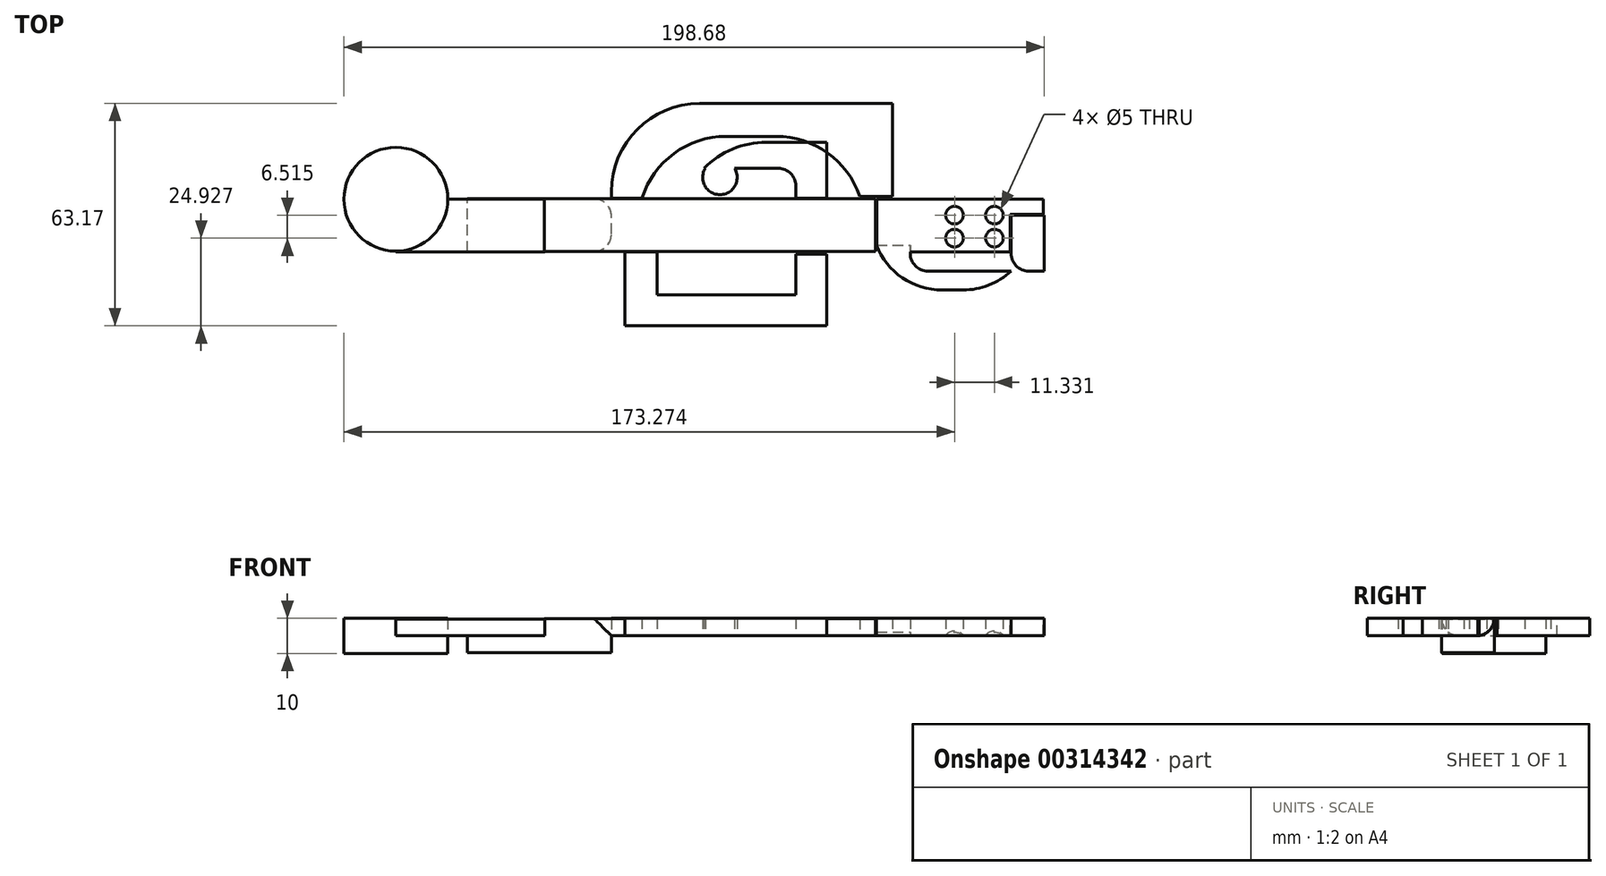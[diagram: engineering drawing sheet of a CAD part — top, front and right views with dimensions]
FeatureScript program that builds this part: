
annotation { "Feature Type Name" : "Feature", "Feature Type Description" : "" }
export const myFeature = defineFeature(function(context is Context, id is Id, definition is map)
    precondition{}
    {
        {
            var Q0;
            Q0=qCreatedBy(makeId("Front.planeOp"),FACE);
            var sketch = newSketch(context, id + "F0", { "sketchPlane" : qUnion([Q0])});
            skLineSegment(sketch, "E0.bottom", {"start": v(0, 0) * mm, "end": v(74.96, 0) * mm});
            skLineSegment(sketch, "E0.top", {"start": v(0, 4.82) * mm, "end": v(74.96, 4.82) * mm});
            skLineSegment(sketch, "E0.left", {"start": v(0, 0) * mm, "end": v(0, 4.82) * mm});
            skLineSegment(sketch, "E0.right", {"start": v(74.96, 0) * mm, "end": v(74.96, 4.82) * mm});
            skLineSegment(sketch, "E1.bottom", {"start": v(0, 4.82) * mm, "end": v(-19.08, 4.82) * mm});
            skLineSegment(sketch, "E1.top", {"start": v(0, -4.82) * mm, "end": v(-19.08, -4.82) * mm});
            skLineSegment(sketch, "E1.left", {"start": v(0, 4.82) * mm, "end": v(0, -4.82) * mm});
            skLineSegment(sketch, "E1.right", {"start": v(-19.08, 4.82) * mm, "end": v(-19.08, -4.82) * mm});
            skPoint(sketch, "E2.oppositeSnap0", {"position": v(-19.08, 0) * mm});
            skLineSegment(sketch, "E2.bottom", {"start": v(-19.08, -4.82) * mm, "end": v(-40.9, -4.82) * mm});
            skLineSegment(sketch, "E2.top", {"start": v(-19.08, 0) * mm, "end": v(-40.9, 0) * mm});
            skLineSegment(sketch, "E2.left", {"start": v(-19.08, -4.82) * mm, "end": v(-19.08, 0) * mm});
            skLineSegment(sketch, "E2.right", {"start": v(-40.9, -4.82) * mm, "end": v(-40.9, 0) * mm});
            skSolve(sketch);
        }
        {
            var Q0;
            Q0 = qSketchRegion(id + "F0", true);
            extrude(context, id + "F1", {"entities" : qUnion([Q0]), "endBound" : BoundingType.SYMMETRIC, "depth" : 15 * mm});
        }
        {
            var Q0;
            Q0=makeQuery(id+"F1.opExtrude","CAP_EDGE",EDGE,{"disambiguationData":[OSD([sQuery(id+"F0.wireOp",EDGE,"E0.bottom")])],"isStart":false});
            var Q1;
            Q1=makeQuery(id+"F1.opExtrude","CAP_EDGE",EDGE,{"disambiguationData":[OSD([sQuery(id+"F0.wireOp",EDGE,"E0.bottom")])],"isStart":true});
            var Q2;
            Q2=makeQuery(id+"F1.opExtrude","CAP_EDGE",EDGE,{"disambiguationData":[OSD([sQuery(id+"F0.wireOp",EDGE,"E1.left")])],"isStart":false});
            var Q3;
            Q3=makeQuery(id+"F1.opExtrude","CAP_EDGE",EDGE,{"disambiguationData":[OSD([sQuery(id+"F0.wireOp",EDGE,"E1.left")])],"isStart":true});
            fillet(context, id + "F2", {"entities" : qUnion([Q0, Q1, Q2, Q3]), "radius" : 5 * mm, "tangentPropagation" : true, "allowEdgeOverflow" : false});
        }
        {
            var Q0;
            Q0=qCreatedBy(makeId("Top.planeOp"),FACE);
            var sketch = newSketch(context, id + "F3", { "sketchPlane" : qUnion([Q0])});
            skLineSegment(sketch, "E3.bottom", {"start": v(-18.98, -7.65) * mm, "end": v(-61.19, -7.65) * mm});
            skLineSegment(sketch, "E3.top", {"start": v(-18.98, 7.37) * mm, "end": v(-61.19, 7.37) * mm});
            skLineSegment(sketch, "E3.left", {"start": v(-18.98, -7.65) * mm, "end": v(-18.98, 7.37) * mm});
            skLineSegment(sketch, "E3.right", {"start": v(-61.19, -7.65) * mm, "end": v(-61.19, 7.37) * mm});
            skCircle(sketch, "E4", {"center": v(-61.19, 7.37) * mm, "radius": 14.73 * mm});
            skSolve(sketch);
        }
        {
            var Q0;
            {var subQ1=sQuery(id+"F3.wireOp",EDGE,"E3.bottom");Q0=makeQuery(id+"F3.imprint","IMPRINT",FACE,{"disambiguationData":[TD([[makeQuery(id+"F3.imprint","IMPRINT",EDGE,{"derivedFrom":subQ1}),-1.0]])]});}
            extrude(context, id + "F4", {"entities" : qUnion([Q0]), "operationType" : NewBodyOperationType.ADD, "depth" : 4.8 * mm});
        }
        {
            var Q0;
            {var subQ0=sQuery(id+"F3.wireOp",EDGE,"E3.right");var subQ1=sQuery(id+"F3.wireOp",EDGE,"E3.top");var subQ2=makeQuery(id+"F3.imprint","INTERSECT",VERTEX,{"derivedFrom":[subQ1,subQ0]});Q0=makeQuery(id+"F3.imprint","IMPRINT",FACE,{"disambiguationData":[TD([[makeQuery(id+"F3.imprint","IMPRINT",EDGE,{"disambiguationData":[TD([[subQ2,1.0]])],"derivedFrom":subQ1}),-1.0]])]});}
            var Q1;
            {var subQ0=sQuery(id+"F3.wireOp",EDGE,"E3.right");var subQ1=sQuery(id+"F3.wireOp",EDGE,"E3.top");var subQ2=makeQuery(id+"F3.imprint","INTERSECT",VERTEX,{"derivedFrom":[subQ1,subQ0]});Q1=makeQuery(id+"F3.imprint","IMPRINT",FACE,{"disambiguationData":[TD([[makeQuery(id+"F3.imprint","IMPRINT",EDGE,{"disambiguationData":[TD([[subQ2,1.0]])],"derivedFrom":subQ1}),1.0]])]});}
            var Q2;
            Q2=makeQuery(id+"F1.opExtrude","SWEPT_BODY",BODY,{"disambiguationData":[OSD([sQuery(id+"F0.wireOp",EDGE,"E0.bottom"),sQuery(id+"F0.wireOp",EDGE,"E0.top"),sQuery(id+"F0.wireOp",EDGE,"E0.right"),sQuery(id+"F0.wireOp",EDGE,"E1.bottom"),sQuery(id+"F0.wireOp",EDGE,"E1.top"),sQuery(id+"F0.wireOp",EDGE,"E1.left"),sQuery(id+"F0.wireOp",EDGE,"E1.right"),sQuery(id+"F0.wireOp",EDGE,"E2.bottom"),sQuery(id+"F0.wireOp",EDGE,"E2.top"),sQuery(id+"F0.wireOp",EDGE,"E2.right")])]});
            extrude(context, id + "F5", {"entities" : qUnion([Q0, Q1]), "operationType" : NewBodyOperationType.ADD, "endBound" : BoundingType.SYMMETRIC, "endBoundEntityBody" : qUnion([Q2]), "depth" : 10 * mm});
        }
        {
            var Q0;
            Q0=qCreatedBy(makeId("Top.planeOp"),FACE);
            var sketch = newSketch(context, id + "F6", { "sketchPlane" : qUnion([Q0])});
            skLineSegment(sketch, "E5.bottom", {"start": v(75.26, -7.65) * mm, "end": v(113.13, -7.65) * mm});
            skLineSegment(sketch, "E5.top", {"start": v(75.26, 7.37) * mm, "end": v(113.13, 7.37) * mm});
            skLineSegment(sketch, "E5.left", {"start": v(75.26, -7.65) * mm, "end": v(75.26, 7.37) * mm});
            skLineSegment(sketch, "E5.right", {"start": v(113.13, -7.65) * mm, "end": v(113.13, 7.37) * mm});
            skLineSegment(sketch, "E6.bottom", {"start": v(113.13, 7.37) * mm, "end": v(122.57, 7.37) * mm});
            skLineSegment(sketch, "E6.top", {"start": v(113.13, 3.12) * mm, "end": v(122.57, 3.12) * mm});
            skLineSegment(sketch, "E6.left", {"start": v(113.13, 7.37) * mm, "end": v(113.13, 3.12) * mm});
            skLineSegment(sketch, "E6.right", {"start": v(122.57, 7.37) * mm, "end": v(122.57, 3.12) * mm});
            skSolve(sketch);
        }
        {
            var Q0;
            Q0=makeQuery(id+"F6.imprint","IMPRINT",FACE,{"disambiguationData":[TD([[makeQuery(id+"F6.imprint","IMPRINT",EDGE,{"derivedFrom":sQuery(id+"F6.wireOp",EDGE,"E5.bottom")}),1.0]])]});
            var Q1;
            Q1=makeQuery(id+"F6.imprint","IMPRINT",FACE,{"disambiguationData":[TD([[makeQuery(id+"F6.imprint","IMPRINT",EDGE,{"derivedFrom":sQuery(id+"F6.wireOp",EDGE,"E6.bottom")}),-1.0]])]});
            extrude(context, id + "F7", {"entities" : qUnion([Q0, Q1]), "depth" : 5 * mm});
        }
        {
            var Q0;
            Q0=makeQuery(id+"F7.opExtrude","CAP_EDGE",EDGE,{"disambiguationData":[OSD([sQuery(id+"F6.wireOp",EDGE,"E5.bottom")])],"isStart":true});
            var Q1;
            Q1=makeQuery(id+"F7.opExtrude","CAP_EDGE",EDGE,{"disambiguationData":[OSD([sQuery(id+"F6.wireOp",EDGE,"E5.top"),sQuery(id+"F6.wireOp",EDGE,"E6.bottom")])],"isStart":true});
            fillet(context, id + "F8", {"entities" : qUnion([Q0, Q1]), "radius" : 5 * mm, "tangentPropagation" : true, "allowEdgeOverflow" : false});
        }
        {
            var Q0;
            Q0=qCreatedBy(makeId("Top.planeOp"),FACE);
            var sketch = newSketch(context, id + "F9", { "sketchPlane" : qUnion([Q0])});
            skLineSegment(sketch, "E7.bottom", {"start": v(113.4, 2.83) * mm, "end": v(122.76, 2.83) * mm});
            skLineSegment(sketch, "E7.top", {"start": v(113.4, -8.21) * mm, "end": v(122.76, -8.21) * mm});
            skLineSegment(sketch, "E7.left", {"start": v(113.4, 2.83) * mm, "end": v(113.4, -8.21) * mm});
            skLineSegment(sketch, "E7.right", {"start": v(122.76, 2.83) * mm, "end": v(122.76, -8.21) * mm});
            skLineSegment(sketch, "E8.bottom", {"start": v(113.4, -2.7) * mm, "end": v(122.76, -2.7) * mm});
            skLineSegment(sketch, "E8.top", {"start": v(113.4, -18.41) * mm, "end": v(122.76, -18.41) * mm});
            skLineSegment(sketch, "E8.left", {"start": v(113.4, -2.7) * mm, "end": v(113.4, -18.41) * mm});
            skLineSegment(sketch, "E8.right", {"start": v(122.76, -2.7) * mm, "end": v(122.76, -18.41) * mm});
            skLineSegment(sketch, "E9.bottom", {"start": v(75.45, -13.03) * mm, "end": v(122.76, -13.03) * mm});
            skLineSegment(sketch, "E9.top", {"start": v(75.45, -18.41) * mm, "end": v(122.76, -18.41) * mm});
            skLineSegment(sketch, "E9.left", {"start": v(75.45, -13.03) * mm, "end": v(75.45, -18.41) * mm});
            skLineSegment(sketch, "E9.right", {"start": v(122.76, -13.03) * mm, "end": v(122.76, -18.41) * mm});
            skLineSegment(sketch, "E10.bottom", {"start": v(75.17, -5.67) * mm, "end": v(84.8, -5.67) * mm});
            skLineSegment(sketch, "E10.top", {"start": v(75.17, -18.41) * mm, "end": v(84.8, -18.41) * mm});
            skLineSegment(sketch, "E10.left", {"start": v(75.17, -5.67) * mm, "end": v(75.17, -18.41) * mm});
            skLineSegment(sketch, "E10.right", {"start": v(84.8, -5.67) * mm, "end": v(84.8, -18.41) * mm});
            skSolve(sketch);
        }
        {
            var Q0;
            {var subQ0=sQuery(id+"F9.wireOp",EDGE,"E9.left");Q0=makeQuery(id+"F9.imprint","IMPRINT",FACE,{"disambiguationData":[TD([[makeQuery(id+"F9.imprint","IMPRINT",EDGE,{"derivedFrom":subQ0}),1.0]])]});}
            var Q1;
            {var subQ1=sQuery(id+"F9.wireOp",EDGE,"E9.left");Q1=makeQuery(id+"F9.imprint","IMPRINT",FACE,{"disambiguationData":[TD([[makeQuery(id+"F9.imprint","IMPRINT",EDGE,{"derivedFrom":subQ1}),-1.0]])]});}
            var Q2;
            {var subQ5=sQuery(id+"F9.wireOp",EDGE,"E9.right");Q2=makeQuery(id+"F9.imprint","IMPRINT",FACE,{"disambiguationData":[TD([[makeQuery(id+"F9.imprint","IMPRINT",EDGE,{"derivedFrom":subQ5}),-1.0]])]});}
            var Q3;
            {var subQ0=sQuery(id+"F9.wireOp",EDGE,"E7.top");Q3=makeQuery(id+"F9.imprint","IMPRINT",FACE,{"disambiguationData":[TD([[makeQuery(id+"F9.imprint","IMPRINT",EDGE,{"derivedFrom":subQ0}),-1.0]])]});}
            var Q4;
            {var subQ0=sQuery(id+"F9.wireOp",EDGE,"E7.top");Q4=makeQuery(id+"F9.imprint","IMPRINT",FACE,{"disambiguationData":[TD([[makeQuery(id+"F9.imprint","IMPRINT",EDGE,{"derivedFrom":subQ0}),1.0]])]});}
            var Q5;
            Q5=makeQuery(id+"F9.imprint","IMPRINT",FACE,{"disambiguationData":[TD([[makeQuery(id+"F9.imprint","IMPRINT",EDGE,{"derivedFrom":sQuery(id+"F9.wireOp",EDGE,"E7.bottom")}),-1.0]])]});
            var Q6;
            {var subQ0=sQuery(id+"F9.wireOp",EDGE,"E9.top");var subQ1=sQuery(id+"F9.wireOp",EDGE,"E8.left");var subQ2=makeQuery(id+"F9.imprint","INTERSECT",VERTEX,{"derivedFrom":[subQ1,subQ0]});Q6=makeQuery(id+"F9.imprint","IMPRINT",FACE,{"disambiguationData":[TD([[makeQuery(id+"F9.imprint","IMPRINT",EDGE,{"disambiguationData":[TD([[subQ2,1.0]])],"derivedFrom":subQ1}),-1.0]])]});}
            extrude(context, id + "F10", {"entities" : qUnion([Q0, Q1, Q2, Q3, Q4, Q5, Q6]), "operationType" : NewBodyOperationType.ADD, "depth" : 5 * mm});
        }
        {
            var Q0;
            Q0=makeQuery(id+"F10.opExtrude","SWEPT_EDGE",EDGE,{"disambiguationData":[OSD([sQuery(id+"F9.wireOp",EDGE,"E10.top"),sQuery(id+"F9.wireOp",EDGE,"E10.left")])]});
            var Q1;
            Q1=makeQuery(id+"F10.opExtrude","SWEPT_EDGE",EDGE,{"disambiguationData":[OSD([sQuery(id+"F9.wireOp",EDGE,"E9.top"),sQuery(id+"F9.wireOp",EDGE,"E9.right")])]});
            fillet(context, id + "F11", {"entities" : qUnion([Q0, Q1]), "radius" : 20 * mm, "tangentPropagation" : true, "allowEdgeOverflow" : false});
        }
        {
            var Q0;
            Q0=qCreatedBy(makeId("Top.planeOp"),FACE);
            var sketch = newSketch(context, id + "F12", { "sketchPlane" : qUnion([Q0])});
            skPoint(sketch, "E11", {"position": v(108.68, 2.83) * mm});
            skPoint(sketch, "E12", {"position": v(108.68, -3.68) * mm});
            skPoint(sketch, "E13", {"position": v(97.35, -3.68) * mm});
            skPoint(sketch, "E14", {"position": v(97.35, 2.83) * mm});
            skSolve(sketch);
        }
        {
            var Q0;
            Q0=sQuery(id+"F12.wireOp",VERTEX,"E14");
            var Q1;
            Q1=makeQuery(id+"F7.opExtrude","SWEPT_BODY",BODY,{"disambiguationData":[OSD([sQuery(id+"F6.wireOp",EDGE,"E5.bottom"),sQuery(id+"F6.wireOp",EDGE,"E5.top"),sQuery(id+"F6.wireOp",EDGE,"E5.left"),sQuery(id+"F6.wireOp",EDGE,"E5.right"),sQuery(id+"F6.wireOp",EDGE,"E6.bottom"),sQuery(id+"F6.wireOp",EDGE,"E6.top"),sQuery(id+"F6.wireOp",EDGE,"E6.right")])]});
            hole(context, id + "F13", {"style" : HoleStyle.SIMPLE, "endStyle" : HoleEndStyle.THROUGH, "oppositeDirection" : true, "holeDiameter" : 5 * mm, "tappedDepth" : 12 * mm, "tapClearance" : 3, "locations" : qUnion([Q0]), "scope" : qUnion([Q1])});
        }
        {
            var Q0;
            Q0=sQuery(id+"F12.wireOp",VERTEX,"E13");
            var Q1;
            Q1=makeQuery(id+"F7.opExtrude","SWEPT_BODY",BODY,{"disambiguationData":[OSD([sQuery(id+"F6.wireOp",EDGE,"E5.bottom"),sQuery(id+"F6.wireOp",EDGE,"E5.top"),sQuery(id+"F6.wireOp",EDGE,"E5.left"),sQuery(id+"F6.wireOp",EDGE,"E5.right"),sQuery(id+"F6.wireOp",EDGE,"E6.bottom"),sQuery(id+"F6.wireOp",EDGE,"E6.top"),sQuery(id+"F6.wireOp",EDGE,"E6.right")])]});
            hole(context, id + "F14", {"style" : HoleStyle.SIMPLE, "endStyle" : HoleEndStyle.THROUGH, "oppositeDirection" : true, "holeDiameter" : 5 * mm, "tappedDepth" : 12 * mm, "tapClearance" : 3, "locations" : qUnion([Q0]), "scope" : qUnion([Q1])});
        }
        {
            var Q0;
            Q0=sQuery(id+"F12.wireOp",VERTEX,"E11");
            var Q1;
            Q1=makeQuery(id+"F7.opExtrude","SWEPT_BODY",BODY,{"disambiguationData":[OSD([sQuery(id+"F6.wireOp",EDGE,"E5.bottom"),sQuery(id+"F6.wireOp",EDGE,"E5.top"),sQuery(id+"F6.wireOp",EDGE,"E5.left"),sQuery(id+"F6.wireOp",EDGE,"E5.right"),sQuery(id+"F6.wireOp",EDGE,"E6.bottom"),sQuery(id+"F6.wireOp",EDGE,"E6.top"),sQuery(id+"F6.wireOp",EDGE,"E6.right")])]});
            hole(context, id + "F15", {"style" : HoleStyle.SIMPLE, "endStyle" : HoleEndStyle.THROUGH, "oppositeDirection" : true, "holeDiameter" : 5 * mm, "tappedDepth" : 12 * mm, "tapClearance" : 3, "locations" : qUnion([Q0]), "scope" : qUnion([Q1])});
        }
        {
            var Q0;
            Q0=sQuery(id+"F12.wireOp",VERTEX,"E12");
            var Q1;
            Q1=makeQuery(id+"F7.opExtrude","SWEPT_BODY",BODY,{"disambiguationData":[OSD([sQuery(id+"F6.wireOp",EDGE,"E5.bottom"),sQuery(id+"F6.wireOp",EDGE,"E5.top"),sQuery(id+"F6.wireOp",EDGE,"E5.left"),sQuery(id+"F6.wireOp",EDGE,"E5.right"),sQuery(id+"F6.wireOp",EDGE,"E6.bottom"),sQuery(id+"F6.wireOp",EDGE,"E6.top"),sQuery(id+"F6.wireOp",EDGE,"E6.right")])]});
            hole(context, id + "F16", {"style" : HoleStyle.SIMPLE, "endStyle" : HoleEndStyle.THROUGH, "oppositeDirection" : true, "holeDiameter" : 5 * mm, "tappedDepth" : 12 * mm, "tapClearance" : 3, "locations" : qUnion([Q0]), "scope" : qUnion([Q1])});
        }
        {
            var Q0;
            Q0=qCreatedBy(makeId("Top.planeOp"),FACE);
            var sketch = newSketch(context, id + "F17", { "sketchPlane" : qUnion([Q0])});
            skLineSegment(sketch, "E15.bottom", {"start": v(70.44, 8.21) * mm, "end": v(79.8, 8.21) * mm});
            skLineSegment(sketch, "E15.top", {"start": v(70.44, 34.56) * mm, "end": v(79.8, 34.56) * mm});
            skLineSegment(sketch, "E15.left", {"start": v(70.44, 8.21) * mm, "end": v(70.44, 34.56) * mm});
            skLineSegment(sketch, "E15.right", {"start": v(79.8, 8.21) * mm, "end": v(79.8, 34.56) * mm});
            skLineSegment(sketch, "E16.bottom", {"start": v(79.8, 34.56) * mm, "end": v(8.69, 34.56) * mm});
            skLineSegment(sketch, "E16.top", {"start": v(79.8, 25.21) * mm, "end": v(8.69, 25.21) * mm});
            skLineSegment(sketch, "E16.left", {"start": v(79.8, 34.56) * mm, "end": v(79.8, 25.21) * mm});
            skLineSegment(sketch, "E16.right", {"start": v(8.69, 34.56) * mm, "end": v(8.69, 25.21) * mm});
            skLineSegment(sketch, "E17.bottom", {"start": v(8.69, 34.56) * mm, "end": v(0, 34.56) * mm});
            skLineSegment(sketch, "E17.top", {"start": v(8.69, 7.65) * mm, "end": v(0, 7.65) * mm});
            skLineSegment(sketch, "E17.left", {"start": v(8.69, 34.56) * mm, "end": v(8.69, 7.65) * mm});
            skLineSegment(sketch, "E17.right", {"start": v(0, 34.56) * mm, "end": v(0, 7.65) * mm});
            skLineSegment(sketch, "E18.bottom", {"start": v(3.87, -7.65) * mm, "end": v(12.94, -7.65) * mm});
            skLineSegment(sketch, "E18.top", {"start": v(3.87, -28.61) * mm, "end": v(12.94, -28.61) * mm});
            skLineSegment(sketch, "E18.left", {"start": v(3.87, -7.65) * mm, "end": v(3.87, -28.61) * mm});
            skLineSegment(sketch, "E18.right", {"start": v(12.94, -7.65) * mm, "end": v(12.94, -28.61) * mm});
            skLineSegment(sketch, "E19.bottom", {"start": v(3.87, -28.61) * mm, "end": v(61.1, -28.61) * mm});
            skLineSegment(sketch, "E19.top", {"start": v(3.87, -19.83) * mm, "end": v(61.1, -19.83) * mm});
            skLineSegment(sketch, "E19.left", {"start": v(3.87, -28.61) * mm, "end": v(3.87, -19.83) * mm});
            skLineSegment(sketch, "E19.right", {"start": v(61.1, -28.61) * mm, "end": v(61.1, -19.83) * mm});
            skLineSegment(sketch, "E20.bottom", {"start": v(61.1, -28.61) * mm, "end": v(52.31, -28.61) * mm});
            skLineSegment(sketch, "E20.top", {"start": v(61.1, -8.21) * mm, "end": v(52.31, -8.21) * mm});
            skLineSegment(sketch, "E20.left", {"start": v(61.1, -28.61) * mm, "end": v(61.1, -8.21) * mm});
            skLineSegment(sketch, "E20.right", {"start": v(52.31, -28.61) * mm, "end": v(52.31, -8.21) * mm});
            skLineSegment(sketch, "E21.bottom", {"start": v(52.31, 7.65) * mm, "end": v(61.1, 7.65) * mm});
            skLineSegment(sketch, "E21.top", {"start": v(52.31, 23.54) * mm, "end": v(61.1, 23.54) * mm});
            skLineSegment(sketch, "E21.left", {"start": v(52.31, 7.65) * mm, "end": v(52.31, 23.54) * mm});
            skLineSegment(sketch, "E21.right", {"start": v(61.1, 7.65) * mm, "end": v(61.1, 23.54) * mm});
            skLineSegment(sketch, "E22.bottom", {"start": v(61.1, 23.54) * mm, "end": v(26.25, 23.54) * mm});
            skLineSegment(sketch, "E22.top", {"start": v(61.1, 16.16) * mm, "end": v(26.25, 16.16) * mm});
            skLineSegment(sketch, "E22.left", {"start": v(61.1, 23.54) * mm, "end": v(61.1, 16.16) * mm});
            skLineSegment(sketch, "E22.right", {"start": v(26.25, 23.54) * mm, "end": v(26.25, 16.16) * mm});
            skSolve(sketch);
        }
        {
            var Q0;
            Q0 = qSketchRegion(id + "F17", true);
            extrude(context, id + "F18", {"entities" : qUnion([Q0]), "depth" : 5 * mm});
        }
        {
            var Q0;
            Q0=makeQuery(id+"F18.opExtrude","SWEPT_EDGE",EDGE,{"disambiguationData":[OSD([sQuery(id+"F17.wireOp",EDGE,"E16.bottom"),sQuery(id+"F17.wireOp",EDGE,"E16.left")])]});
            var Q1;
            Q1=makeQuery(id+"F18.opExtrude","SWEPT_EDGE",EDGE,{"disambiguationData":[OSD([sQuery(id+"F17.wireOp",EDGE,"E17.bottom"),sQuery(id+"F17.wireOp",EDGE,"E17.right")])]});
            var Q2;
            Q2=makeQuery(id+"F18.opExtrude","SWEPT_EDGE",EDGE,{"disambiguationData":[OSD([sQuery(id+"F17.wireOp",EDGE,"E20.bottom"),sQuery(id+"F17.wireOp",EDGE,"E20.left")])]});
            var Q3;
            Q3=makeQuery(id+"F18.opExtrude","SWEPT_EDGE",EDGE,{"disambiguationData":[OSD([sQuery(id+"F17.wireOp",EDGE,"E16.top"),sQuery(id+"F17.wireOp",EDGE,"E17.left")])]});
            var Q4;
            Q4=makeQuery(id+"F18.opExtrude","SWEPT_EDGE",EDGE,{"disambiguationData":[OSD([sQuery(id+"F17.wireOp",EDGE,"E15.left"),sQuery(id+"F17.wireOp",EDGE,"E16.top")])]});
            var Q5;
            Q5=makeQuery(id+"F18.opExtrude","SWEPT_EDGE",EDGE,{"disambiguationData":[OSD([sQuery(id+"F17.wireOp",EDGE,"E19.top"),sQuery(id+"F17.wireOp",EDGE,"E20.right")])]});
            var Q6;
            Q6=makeQuery(id+"F18.opExtrude","SWEPT_EDGE",EDGE,{"disambiguationData":[OSD([sQuery(id+"F17.wireOp",EDGE,"E18.right"),sQuery(id+"F17.wireOp",EDGE,"E19.top")])]});
            var Q7;
            Q7=makeQuery(id+"F18.opExtrude","SWEPT_EDGE",EDGE,{"disambiguationData":[OSD([sQuery(id+"F17.wireOp",EDGE,"E22.bottom"),sQuery(id+"F17.wireOp",EDGE,"E22.left")])]});
            var Q8;
            Q8=makeQuery(id+"F18.opExtrude","SWEPT_EDGE",EDGE,{"disambiguationData":[OSD([sQuery(id+"F17.wireOp",EDGE,"E22.bottom"),sQuery(id+"F17.wireOp",EDGE,"E22.right")])]});
            var Q9;
            Q9=makeQuery(id+"F18.opExtrude","SWEPT_EDGE",EDGE,{"disambiguationData":[OSD([sQuery(id+"F17.wireOp",EDGE,"E19.bottom"),sQuery(id+"F17.wireOp",EDGE,"E19.left")])]});
            fillet(context, id + "F19", {"entities" : qUnion([Q0, Q1, Q2, Q3, Q4, Q5, Q6, Q7, Q8, Q9]), "radius" : 25 * mm, "tangentPropagation" : true, "allowEdgeOverflow" : false});
        }
        {
            var Q0;
            Q0=qCreatedBy(makeId("Top.planeOp"),FACE);
            var sketch = newSketch(context, id + "F20", { "sketchPlane" : qUnion([Q0])});
            skCircle(sketch, "E23", {"center": v(30.78, 13.57) * mm, "radius": 4.9 * mm});
            skSolve(sketch);
        }
        {
            var Q0;
            Q0=makeQuery(id+"F20.imprint","IMPRINT",FACE,{"disambiguationData":[TD([[makeQuery(id+"F20.imprint","IMPRINT",EDGE,{"derivedFrom":sQuery(id+"F20.wireOp",EDGE,"E23")}),1.0]])]});
            extrude(context, id + "F21", {"entities" : qUnion([Q0]), "operationType" : NewBodyOperationType.ADD, "depth" : 5 * mm});
        }
        {
            var Q0;
            Q0=makeQuery(id+"F10.opExtrude","SWEPT_EDGE",EDGE,{"disambiguationData":[OSD([sQuery(id+"F9.wireOp",EDGE,"E8.left"),sQuery(id+"F9.wireOp",EDGE,"E9.bottom")])]});
            var Q1;
            Q1=makeQuery(id+"F10.opExtrude","SWEPT_EDGE",EDGE,{"disambiguationData":[OSD([sQuery(id+"F9.wireOp",EDGE,"E9.bottom"),sQuery(id+"F9.wireOp",EDGE,"E10.right")])]});
            var Q2;
            Q2=makeQuery(id+"F18.opExtrude","SWEPT_EDGE",EDGE,{"disambiguationData":[OSD([sQuery(id+"F17.wireOp",EDGE,"E21.left"),sQuery(id+"F17.wireOp",EDGE,"E22.top")])]});
            fillet(context, id + "F22", {"entities" : qUnion([Q0, Q1, Q2]), "radius" : 5 * mm, "tangentPropagation" : true, "allowEdgeOverflow" : false});
        }
    });
